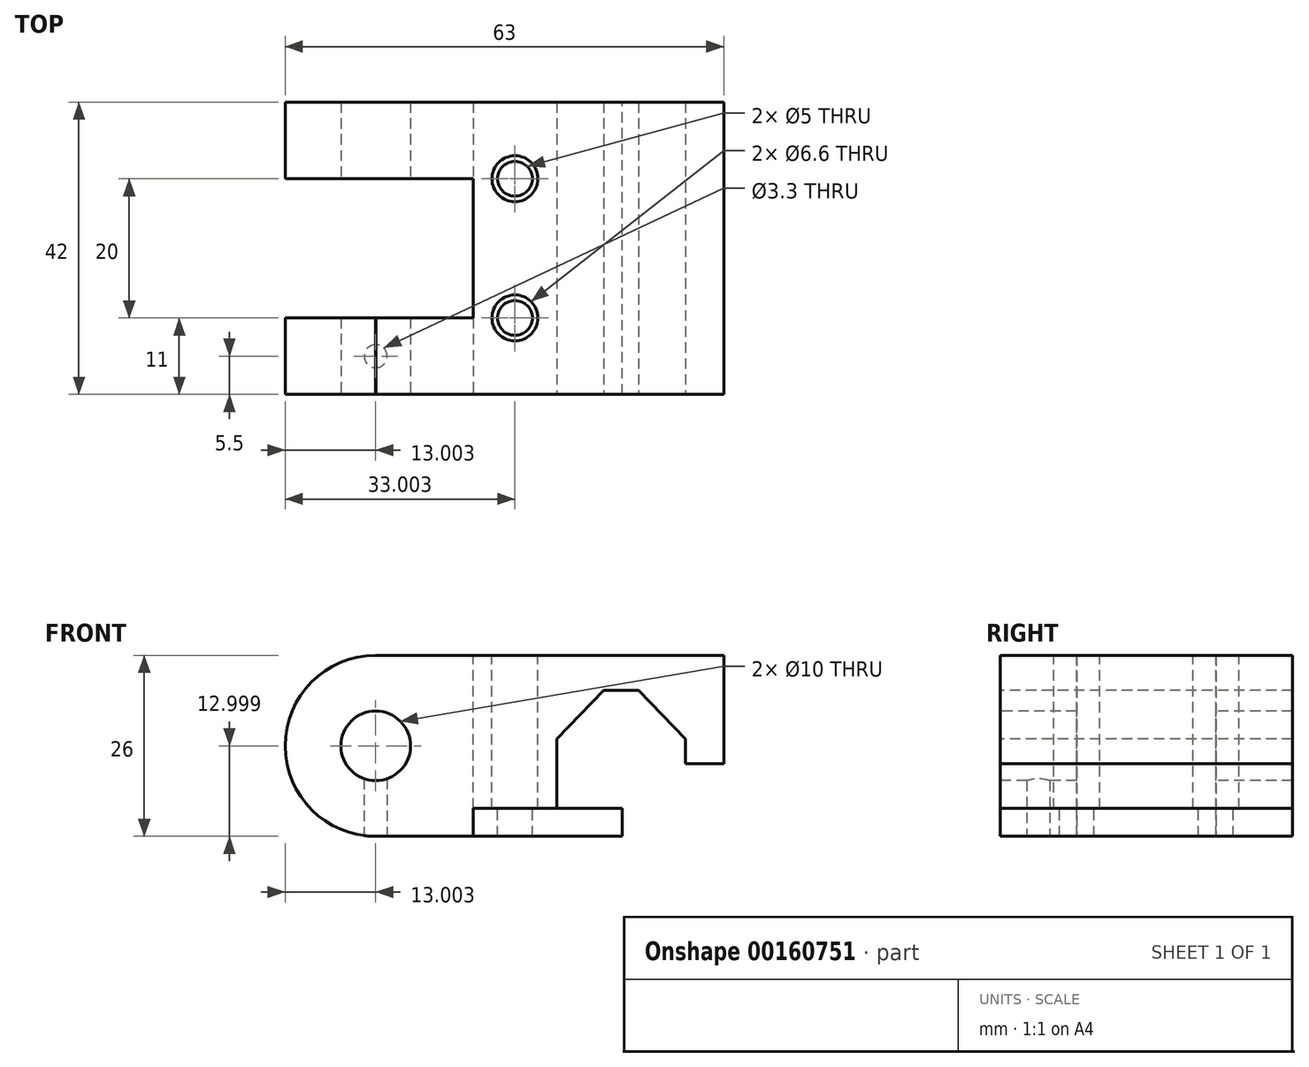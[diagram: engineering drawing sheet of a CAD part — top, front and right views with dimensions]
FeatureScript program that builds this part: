
annotation { "Feature Type Name" : "Feature", "Feature Type Description" : "" }
export const myFeature = defineFeature(function(context is Context, id is Id, definition is map)
    precondition{}
    {
        {
            var Q0;
            Q0=qCreatedBy(makeId("Front.planeOp"),FACE);
            var sketch = newSketch(context, id + "F0", { "sketchPlane" : qUnion([Q0])});
            skLineSegment(sketch, "E0", {"start": v(10.4, 7.7) * mm, "end": v(15.4, 7.7) * mm});
            skLineSegment(sketch, "E1", {"start": v(15.4, 7.7) * mm, "end": v(22.14, 0.7) * mm});
            skLineSegment(sketch, "E2", {"start": v(-22.36, 12.7) * mm, "end": v(27.64, 12.7) * mm});
            skLineSegment(sketch, "E3", {"start": v(-8.36, -13.3) * mm, "end": v(-22.36, -13.3) * mm});
            skLineSegment(sketch, "E4", {"start": v(22.14, -2.88) * mm, "end": v(27.64, -2.88) * mm});
            skLineSegment(sketch, "E5", {"start": v(22.14, -2.88) * mm, "end": v(22.14, 0.7) * mm});
            skLineSegment(sketch, "E6", {"start": v(10.4, 7.7) * mm, "end": v(3.64, 0.7) * mm});
            skLineSegment(sketch, "E7", {"start": v(3.64, 0.7) * mm, "end": v(3.64, -9.3) * mm});
            skLineSegment(sketch, "E8", {"start": v(27.64, -2.88) * mm, "end": v(27.64, 12.7) * mm});
            skLineSegment(sketch, "E9", {"start": v(-22.36, 18.7) * mm, "end": v(-22.36, -23.6) * mm, "construction": true});
            skLineSegment(sketch, "E10", {"start": v(-33.44, -0.3) * mm, "end": v(-7.35, -0.3) * mm, "construction": true});
            skCircle(sketch, "E11", {"center": v(-22.36, -0.3) * mm, "radius": 5 * mm});
            skArc(sketch, "E12", {"start": v(-22.36, 12.7) * mm, "mid": v(-35.36, -0.3) * mm, "end": v(-22.36, -13.3) * mm});
            skPoint(sketch, "E13.orphan", {"position": v(-36.36, -13.3) * mm});
            skLineSegment(sketch, "E14", {"start": v(-8.36, -9.3) * mm, "end": v(3.64, -9.3) * mm});
            skLineSegment(sketch, "E15", {"start": v(-8.36, -9.3) * mm, "end": v(-8.36, -13.3) * mm});
            skLineSegment(sketch, "E16", {"start": v(-2.36, -9.3) * mm, "end": v(-2.36, 20.11) * mm, "construction": true});
            skSolve(sketch);
        }
        {
            var Q0;
            Q0=makeQuery(id+"F0.imprint","IMPRINT",FACE,{"disambiguationData":[TD([[makeQuery(id+"F0.imprint","IMPRINT",EDGE,{"derivedFrom":sQuery(id+"F0.wireOp",EDGE,"E0")}),1.0]])]});
            extrude(context, id + "F1", {"entities" : qUnion([Q0]), "oppositeDirection" : true, "depth" : 42 * mm});
        }
        {
            var Q0;
            Q0=makeQuery(id+"F1.opExtrude","SWEPT_FACE",FACE,{"disambiguationData":[OSD([sQuery(id+"F0.wireOp",EDGE,"E2")])]});
            var sketch = newSketch(context, id + "F2", { "sketchPlane" : qUnion([Q0])});
            skLineSegment(sketch, "E17", {"start": v(-37.57, 31) * mm, "end": v(-8.36, 31) * mm});
            skLineSegment(sketch, "E18", {"start": v(-37.48, 11) * mm, "end": v(-8.36, 11) * mm});
            skLineSegment(sketch, "E19", {"start": v(-8.36, 31) * mm, "end": v(-8.36, 11) * mm});
            skLineSegment(sketch, "E20", {"start": v(-37.57, 31) * mm, "end": v(-37.48, 11) * mm});
            skSolve(sketch);
        }
        {
            var Q0;
            {var subQ0=sQuery(id+"F2.wireOp",EDGE,"E20");Q0=makeQuery(id+"F2.imprint","IMPRINT",FACE,{"disambiguationData":[TD([[makeQuery(id+"F2.imprint","IMPRINT",EDGE,{"derivedFrom":subQ0}),1.0]])]});}
            var Q1;
            {var subQ0=sQuery(id+"F2.wireOp",EDGE,"E19");Q1=makeQuery(id+"F2.imprint","IMPRINT",FACE,{"disambiguationData":[TD([[makeQuery(id+"F2.imprint","IMPRINT",EDGE,{"derivedFrom":subQ0}),-1.0]])]});}
            extrude(context, id + "F3", {"entities" : qUnion([Q0, Q1]), "operationType" : NewBodyOperationType.REMOVE, "endBound" : BoundingType.THROUGH_ALL, "oppositeDirection" : true, "depth" : 25 * mm});
        }
        {
            var Q0;
            Q0=makeQuery(id+"F1.opExtrude","SWEPT_FACE",FACE,{"disambiguationData":[OSD([sQuery(id+"F0.wireOp",EDGE,"E3")])]});
            var sketch = newSketch(context, id + "F4", { "sketchPlane" : qUnion([Q0])});
            skPoint(sketch, "E21", {"position": v(-22.36, -5.5) * mm});
            skSolve(sketch);
        }
        {
            var Q0;
            Q0=sQuery(id+"F4.wireOp",VERTEX,"E21");
            var Q1;
            Q1=makeQuery(id+"F1.opExtrude","SWEPT_BODY",BODY,{"disambiguationData":[OSD([sQuery(id+"F0.wireOp",EDGE,"E0"),sQuery(id+"F0.wireOp",EDGE,"E1"),sQuery(id+"F0.wireOp",EDGE,"E2"),sQuery(id+"F0.wireOp",EDGE,"E3"),sQuery(id+"F0.wireOp",EDGE,"E4"),sQuery(id+"F0.wireOp",EDGE,"E5"),sQuery(id+"F0.wireOp",EDGE,"E6"),sQuery(id+"F0.wireOp",EDGE,"E7"),sQuery(id+"F0.wireOp",EDGE,"E8"),sQuery(id+"F0.wireOp",EDGE,"E11"),sQuery(id+"F0.wireOp",EDGE,"E12")])]});
            hole(context, id + "F5", {"style" : HoleStyle.SIMPLE, "endStyle" : HoleEndStyle.BLIND, "standardTappedOrClearance" : lookupTablePath({ "standard" : "ISO", "fit" : "Normal", "size" : "M3", "type" : "Clearance" }), "standardBlindInLast" : lookupTablePath({ "fit" : "Standard", "standard" : "ISO", "size" : "M3", "type" : "Clearance" }), "holeDiameter" : 3.3 * mm, "holeDepth" : 9 * mm, "locations" : qUnion([Q0]), "scope" : qUnion([Q1])});
        }
        {
            var Q0;
            Q0=makeQuery(id+"F1.opExtrude","SWEPT_FACE",FACE,{"disambiguationData":[OSD([sQuery(id+"F0.wireOp",EDGE,"E2")])]});
            var sketch = newSketch(context, id + "F6", { "sketchPlane" : qUnion([Q0])});
            skPoint(sketch, "E22", {"position": v(-2.36, 31) * mm});
            skPoint(sketch, "E23", {"position": v(-2.36, 11) * mm});
            skSolve(sketch);
        }
        {
            var Q0;
            Q0=sQuery(id+"F6.wireOp",VERTEX,"E22");
            var Q1;
            Q1=sQuery(id+"F6.wireOp",VERTEX,"E23");
            var Q2;
            Q2=makeQuery(id+"F1.opExtrude","SWEPT_BODY",BODY,{"disambiguationData":[OSD([sQuery(id+"F0.wireOp",EDGE,"E0"),sQuery(id+"F0.wireOp",EDGE,"E1"),sQuery(id+"F0.wireOp",EDGE,"E2"),sQuery(id+"F0.wireOp",EDGE,"E3"),sQuery(id+"F0.wireOp",EDGE,"E4"),sQuery(id+"F0.wireOp",EDGE,"E5"),sQuery(id+"F0.wireOp",EDGE,"E6"),sQuery(id+"F0.wireOp",EDGE,"E7"),sQuery(id+"F0.wireOp",EDGE,"E8"),sQuery(id+"F0.wireOp",EDGE,"E11"),sQuery(id+"F0.wireOp",EDGE,"E12"),sQuery(id+"F0.wireOp",EDGE,"E14"),sQuery(id+"F0.wireOp",EDGE,"E15")])]});
            hole(context, id + "F7", {"style" : HoleStyle.SIMPLE, "endStyle" : HoleEndStyle.THROUGH, "standardTappedOrClearance" : lookupTablePath({ "standard" : "ISO", "fit" : "Normal", "size" : "M6", "type" : "Clearance" }), "standardBlindInLast" : lookupTablePath({ "fit" : "Standard", "standard" : "ISO", "size" : "M6", "type" : "Clearance" }), "holeDiameter" : 6.6 * mm, "locations" : qUnion([Q0, Q1]), "scope" : qUnion([Q2]), "isTappedThrough" : true});
        }
        {
            var Q0;
            Q0=makeQuery(id+"F1.opExtrude","SWEPT_FACE",FACE,{"disambiguationData":[OSD([sQuery(id+"F0.wireOp",EDGE,"E14")])]});
            var sketch = newSketch(context, id + "F8", { "sketchPlane" : qUnion([Q0])});
            skLineSegment(sketch, "E24.bottom", {"start": v(-8.36, 0) * mm, "end": v(13.06, 0) * mm});
            skLineSegment(sketch, "E24.top", {"start": v(-8.36, -42) * mm, "end": v(13.06, -42) * mm});
            skLineSegment(sketch, "E24.left", {"start": v(-8.36, 0) * mm, "end": v(-8.36, -42) * mm});
            skLineSegment(sketch, "E24.right", {"start": v(13.06, 0) * mm, "end": v(13.06, -42) * mm});
            skSolve(sketch);
        }
        {
            var Q0;
            Q0 = qSketchRegion(id + "F8", true);
            var Q1;
            {var subQ1=makeQuery(id+"F1.opExtrude","SWEPT_EDGE",EDGE,{"disambiguationData":[OSD([sQuery(id+"F0.wireOp",EDGE,"E7"),sQuery(id+"F0.wireOp",EDGE,"E14")])]});Q1=makeQuery(id+"F8.imprint","IMPRINT",FACE,{"disambiguationData":[TD([[makeQuery(id+"F8.imprint","IMPRINT",EDGE,{"derivedFrom":subQ1}),1.0]])]});}
            extrude(context, id + "F9", {"entities" : qUnion([Q0, Q1]), "depth" : 4 * mm});
        }
        {
            var Q0;
            Q0=sQuery(id+"F6.wireOp",VERTEX,"E23");
            var Q1;
            Q1=sQuery(id+"F6.wireOp",VERTEX,"E22");
            var Q2;
            Q2=makeQuery(id+"F9.opExtrude","SWEPT_BODY",BODY,{"disambiguationData":[OSD([sQuery(id+"F8.wireOp",EDGE,"E24.bottom"),sQuery(id+"F8.wireOp",EDGE,"E24.top"),sQuery(id+"F8.wireOp",EDGE,"E24.left"),sQuery(id+"F8.wireOp",EDGE,"E24.right")])]});
            hole(context, id + "F10", {"style" : HoleStyle.SIMPLE, "endStyle" : HoleEndStyle.THROUGH, "standardTappedOrClearance" : lookupTablePath({ "standard" : "ISO", "engagement" : "75%", "pitch" : "1 mm", "size" : "M6", "type" : "Tapped" }), "standardBlindInLast" : lookupTablePath({ "standard" : "ISO", "engagement" : "75%", "pitch" : "1 mm", "size" : "M6", "type" : "Tapped" }), "holeDiameter" : 5 * mm, "locations" : qUnion([Q0, Q1]), "scope" : qUnion([Q2]), "isTappedThrough" : true, "majorDiameter" : 6 * mm, "showTappedDepth" : true});
        }
        {
            var Q0;
            Q0=makeQuery(id+"F1.opExtrude","CAP_FACE",FACE,{"disambiguationData":[OSD([sQuery(id+"F0.wireOp",EDGE,"E0"),sQuery(id+"F0.wireOp",EDGE,"E1"),sQuery(id+"F0.wireOp",EDGE,"E2"),sQuery(id+"F0.wireOp",EDGE,"E3"),sQuery(id+"F0.wireOp",EDGE,"E4"),sQuery(id+"F0.wireOp",EDGE,"E5"),sQuery(id+"F0.wireOp",EDGE,"E6"),sQuery(id+"F0.wireOp",EDGE,"E7"),sQuery(id+"F0.wireOp",EDGE,"E8"),sQuery(id+"F0.wireOp",EDGE,"E11"),sQuery(id+"F0.wireOp",EDGE,"E12"),sQuery(id+"F0.wireOp",EDGE,"E14"),sQuery(id+"F0.wireOp",EDGE,"E15")])],"isStart":true});
            var sketch = newSketch(context, id + "F11", { "sketchPlane" : qUnion([Q0])});
            skLineSegment(sketch, "E25", {"start": v(-22.4, 12.7) * mm, "end": v(-22.36, 12.55) * mm});
            skLineSegment(sketch, "E26", {"start": v(-22.36, 12.55) * mm, "end": v(-22.32, 12.7) * mm});
            skLineSegment(sketch, "E27", {"start": v(-22.4, 12.7) * mm, "end": v(-22.32, 12.7) * mm});
            skSolve(sketch);
        }
        {
            var Q0;
            {var subQ0=sQuery(id+"F11.wireOp",EDGE,"E25");Q0=makeQuery(id+"F11.imprint","IMPRINT",FACE,{"disambiguationData":[TD([[makeQuery(id+"F11.imprint","IMPRINT",EDGE,{"derivedFrom":subQ0}),1.0]])]});}
            extrude(context, id + "F12", {"entities" : qUnion([Q0]), "operationType" : NewBodyOperationType.REMOVE, "endBound" : BoundingType.UP_TO_NEXT, "oppositeDirection" : true, "depth" : 25 * mm});
        }
    });
